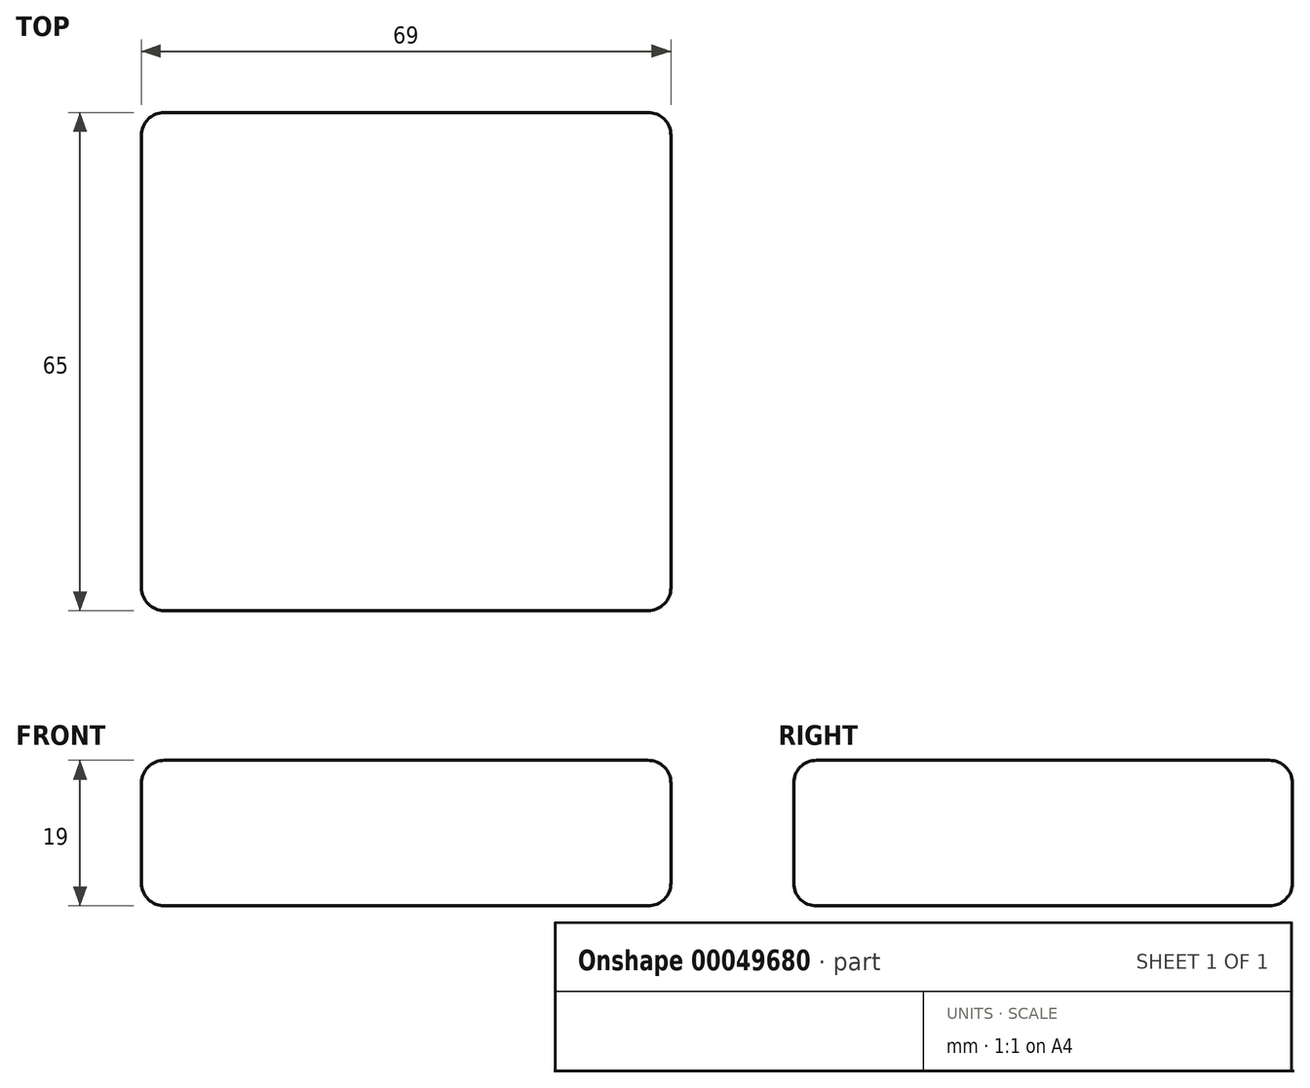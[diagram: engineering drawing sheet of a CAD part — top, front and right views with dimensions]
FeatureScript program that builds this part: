
annotation { "Feature Type Name" : "Feature", "Feature Type Description" : "" }
export const myFeature = defineFeature(function(context is Context, id is Id, definition is map)
    precondition{}
    {
        {
            var Q0;
            Q0=qCreatedBy(makeId("Top.planeOp"),FACE);
            var sketch = newSketch(context, id + "F0", { "sketchPlane" : qUnion([Q0])});
            skLineSegment(sketch, "E0.rect.bottom", {"start": v(-34.5, 32.5) * mm, "end": v(34.5, 32.5) * mm});
            skLineSegment(sketch, "E0.rect.top", {"start": v(-34.5, -32.5) * mm, "end": v(34.5, -32.5) * mm});
            skLineSegment(sketch, "E0.rect.left", {"start": v(-34.5, 32.5) * mm, "end": v(-34.5, -32.5) * mm});
            skLineSegment(sketch, "E0.rect.right", {"start": v(34.5, 32.5) * mm, "end": v(34.5, -32.5) * mm});
            skPoint(sketch, "E0.rect.middle", {"position": v(0, 0) * mm});
            skSolve(sketch);
        }
        {
            var Q0;
            Q0 = qSketchRegion(id + "F0", true);
            extrude(context, id + "F1", {"entities" : qUnion([Q0]), "depth" : 19 * mm});
        }
        {
            var Q0;
            Q0=makeQuery(id+"F1.opExtrude","CAP_EDGE",EDGE,{"disambiguationData":[OSD([sQuery(id+"F0.wireOp",EDGE,"E0.rect.top")])],"isStart":false});
            var Q1;
            Q1=makeQuery(id+"F1.opExtrude","CAP_EDGE",EDGE,{"disambiguationData":[OSD([sQuery(id+"F0.wireOp",EDGE,"E0.rect.left")])],"isStart":false});
            var Q2;
            Q2=makeQuery(id+"F1.opExtrude","CAP_EDGE",EDGE,{"disambiguationData":[OSD([sQuery(id+"F0.wireOp",EDGE,"E0.rect.left")])],"isStart":true});
            var Q3;
            Q3=makeQuery(id+"F1.opExtrude","SWEPT_EDGE",EDGE,{"disambiguationData":[OSD([sQuery(id+"F0.wireOp",EDGE,"E0.rect.top"),sQuery(id+"F0.wireOp",EDGE,"E0.rect.left")])]});
            var Q4;
            Q4=makeQuery(id+"F1.opExtrude","CAP_EDGE",EDGE,{"disambiguationData":[OSD([sQuery(id+"F0.wireOp",EDGE,"E0.rect.top")])],"isStart":true});
            var Q5;
            Q5=makeQuery(id+"F1.opExtrude","SWEPT_EDGE",EDGE,{"disambiguationData":[OSD([sQuery(id+"F0.wireOp",EDGE,"E0.rect.top"),sQuery(id+"F0.wireOp",EDGE,"E0.rect.right")])]});
            var Q6;
            Q6=makeQuery(id+"F1.opExtrude","CAP_EDGE",EDGE,{"disambiguationData":[OSD([sQuery(id+"F0.wireOp",EDGE,"E0.rect.right")])],"isStart":true});
            var Q7;
            Q7=makeQuery(id+"F1.opExtrude","CAP_EDGE",EDGE,{"disambiguationData":[OSD([sQuery(id+"F0.wireOp",EDGE,"E0.rect.right")])],"isStart":false});
            var Q8;
            Q8=makeQuery(id+"F1.opExtrude","CAP_EDGE",EDGE,{"disambiguationData":[OSD([sQuery(id+"F0.wireOp",EDGE,"E0.rect.bottom")])],"isStart":false});
            var Q9;
            Q9=makeQuery(id+"F1.opExtrude","CAP_EDGE",EDGE,{"disambiguationData":[OSD([sQuery(id+"F0.wireOp",EDGE,"E0.rect.bottom")])],"isStart":true});
            var Q10;
            Q10=makeQuery(id+"F1.opExtrude","SWEPT_EDGE",EDGE,{"disambiguationData":[OSD([sQuery(id+"F0.wireOp",EDGE,"E0.rect.bottom"),sQuery(id+"F0.wireOp",EDGE,"E0.rect.left")])]});
            var Q11;
            Q11=makeQuery(id+"F1.opExtrude","SWEPT_EDGE",EDGE,{"disambiguationData":[OSD([sQuery(id+"F0.wireOp",EDGE,"E0.rect.bottom"),sQuery(id+"F0.wireOp",EDGE,"E0.rect.right")])]});
            fillet(context, id + "F2", {"entities" : qUnion([Q0, Q1, Q2, Q3, Q4, Q5, Q6, Q7, Q8, Q9, Q10, Q11]), "radius" : 3 * mm, "tangentPropagation" : true, "allowEdgeOverflow" : false});
        }
    });
